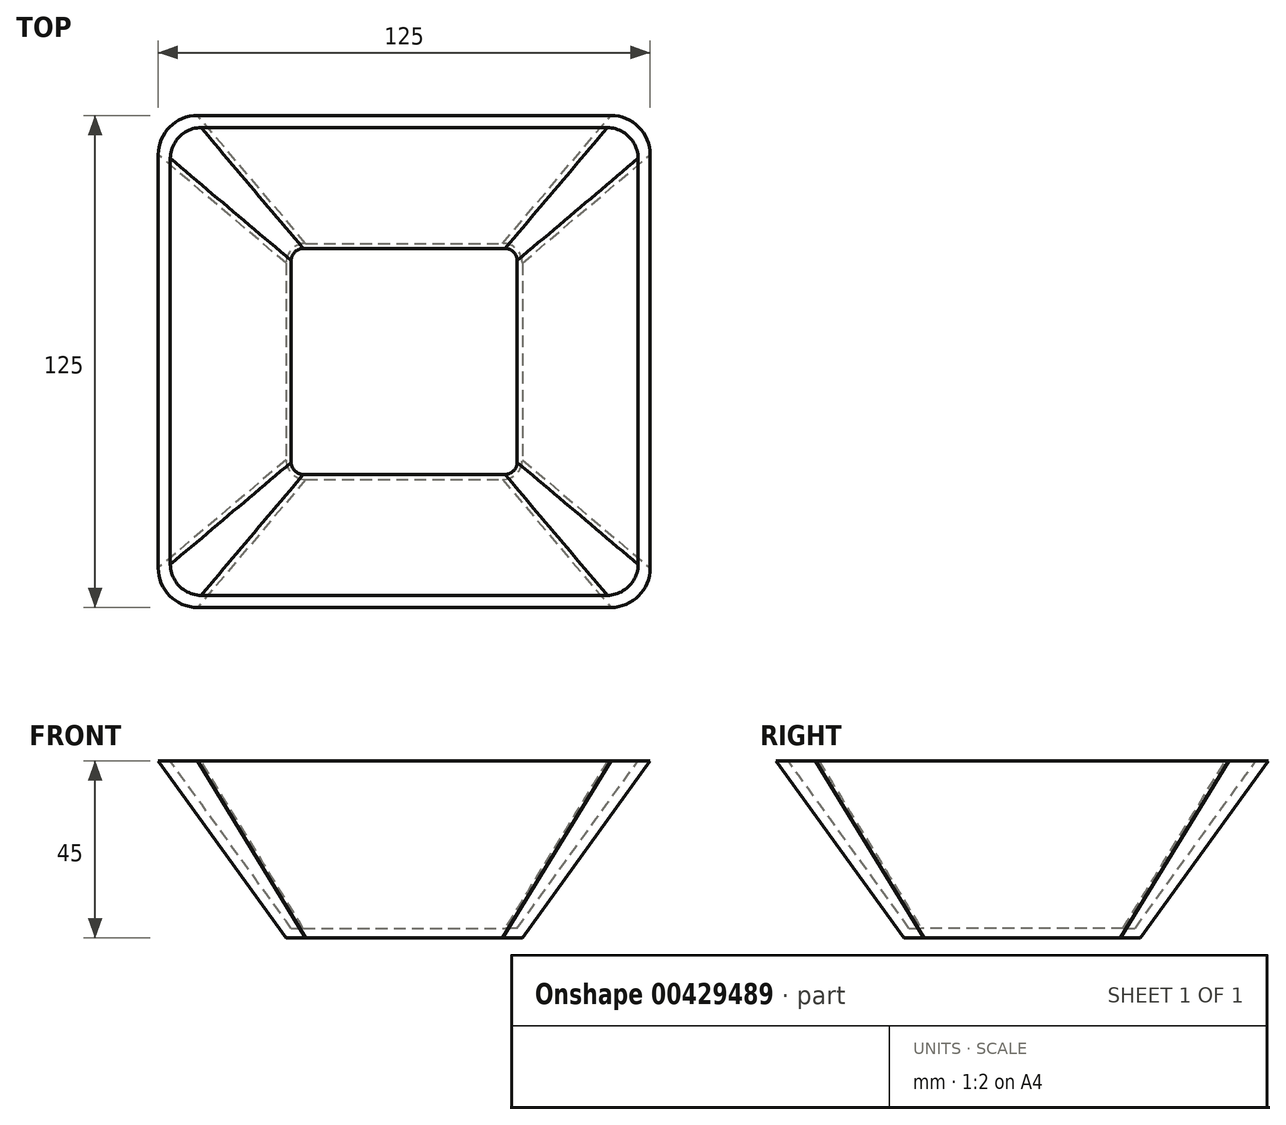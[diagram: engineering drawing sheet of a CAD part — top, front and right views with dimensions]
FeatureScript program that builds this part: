
annotation { "Feature Type Name" : "Feature", "Feature Type Description" : "" }
export const myFeature = defineFeature(function(context is Context, id is Id, definition is map)
    precondition{}
    {
        {
            var Q0;
            Q0=qCreatedBy(makeId("Top.planeOp"),FACE);
            var sketch = newSketch(context, id + "F0", { "sketchPlane" : qUnion([Q0])});
            skLineSegment(sketch, "E0.bottom", {"start": v(-25, 30) * mm, "end": v(25, 30) * mm});
            skLineSegment(sketch, "E0.top", {"start": v(-25, -30) * mm, "end": v(25, -30) * mm});
            skLineSegment(sketch, "E0.left", {"start": v(-30, 25) * mm, "end": v(-30, -25) * mm});
            skLineSegment(sketch, "E0.right", {"start": v(30, 25) * mm, "end": v(30, -25) * mm});
            skLineSegment(sketch, "E1", {"start": v(-30, -30) * mm, "end": v(30, 30) * mm, "construction": true});
            skPoint(sketch, "E2.visualSharp", {"position": v(30, 30) * mm});
            skArc(sketch, "E2.filletArc", {"start": v(30, 25) * mm, "mid": v(28.54, 28.54) * mm, "end": v(25, 30) * mm});
            skPoint(sketch, "E3.visualSharp", {"position": v(-30, 30) * mm});
            skArc(sketch, "E3.filletArc", {"start": v(-25, 30) * mm, "mid": v(-28.54, 28.54) * mm, "end": v(-30, 25) * mm});
            skPoint(sketch, "E4.visualSharp", {"position": v(30, -30) * mm});
            skArc(sketch, "E4.filletArc", {"start": v(25, -30) * mm, "mid": v(28.54, -28.54) * mm, "end": v(30, -25) * mm});
            skPoint(sketch, "E5.visualSharp", {"position": v(-30, -30) * mm});
            skArc(sketch, "E5.filletArc", {"start": v(-30, -25) * mm, "mid": v(-28.54, -28.54) * mm, "end": v(-25, -30) * mm});
            skSolve(sketch);
        }
        {
            var Q0;
            Q0=qCreatedBy(makeId("Top.planeOp"),FACE);
            cPlane(context, id + "F1", {"entities" : qUnion([Q0]), "cplaneType" : CPlaneType.OFFSET, "offset" : 45 * mm, "width" : 150 * mm, "height" : 150 * mm});
        }
        {
            var Q0;
            Q0=qCreatedBy(id+"F1.planeOp",FACE);
            var sketch = newSketch(context, id + "F2", { "sketchPlane" : qUnion([Q0])});
            skLineSegment(sketch, "E6.bottom", {"start": v(-52.5, 62.5) * mm, "end": v(52.5, 62.5) * mm});
            skLineSegment(sketch, "E6.top", {"start": v(-52.5, -62.5) * mm, "end": v(52.5, -62.5) * mm});
            skLineSegment(sketch, "E6.left", {"start": v(-62.5, 52.5) * mm, "end": v(-62.5, -52.5) * mm});
            skLineSegment(sketch, "E6.right", {"start": v(62.5, 52.5) * mm, "end": v(62.5, -52.5) * mm});
            skLineSegment(sketch, "E7", {"start": v(-62.5, 62.5) * mm, "end": v(62.5, -62.5) * mm, "construction": true});
            skPoint(sketch, "E8.visualSharp", {"position": v(62.5, 62.5) * mm});
            skArc(sketch, "E8.filletArc", {"start": v(62.5, 52.5) * mm, "mid": v(59.57, 59.57) * mm, "end": v(52.5, 62.5) * mm});
            skPoint(sketch, "E9.visualSharp", {"position": v(-62.5, 62.5) * mm});
            skArc(sketch, "E9.filletArc", {"start": v(-52.5, 62.5) * mm, "mid": v(-59.57, 59.57) * mm, "end": v(-62.5, 52.5) * mm});
            skPoint(sketch, "E10.visualSharp", {"position": v(-62.5, -62.5) * mm});
            skArc(sketch, "E10.filletArc", {"start": v(-62.5, -52.5) * mm, "mid": v(-59.57, -59.57) * mm, "end": v(-52.5, -62.5) * mm});
            skPoint(sketch, "E11.visualSharp", {"position": v(62.5, -62.5) * mm});
            skArc(sketch, "E11.filletArc", {"start": v(52.5, -62.5) * mm, "mid": v(59.57, -59.57) * mm, "end": v(62.5, -52.5) * mm});
            skSolve(sketch);
        }
        {
            var Q0;
            Q0=makeQuery(id+"F0.imprint","IMPRINT",FACE,{"disambiguationData":[TD([[makeQuery(id+"F0.imprint","IMPRINT",EDGE,{"derivedFrom":sQuery(id+"F0.wireOp",EDGE,"E0.bottom")}),-1.0]])]});
            var Q1;
            Q1=makeQuery(id+"F2.imprint","IMPRINT",FACE,{"disambiguationData":[TD([[makeQuery(id+"F2.imprint","IMPRINT",EDGE,{"derivedFrom":sQuery(id+"F2.wireOp",EDGE,"E6.bottom")}),-1.0]])]});
            loft(context, id + "F3", {"sheetProfilesArray" : [{ "sheetProfileEntities" : qUnion([Q0]) }, { "sheetProfileEntities" : qUnion([Q1]) }]});
        }
        {
            var Q0;
            Q0=makeQuery(id+"F3.opLoft","CAP_FACE",FACE,{"disambiguationData":[OSD([makeQuery(id+"F2.imprint","IMPRINT",FACE,{"disambiguationData":[TD([[makeQuery(id+"F2.imprint","IMPRINT",EDGE,{"derivedFrom":sQuery(id+"F2.wireOp",EDGE,"E6.bottom")}),-1.0]])]})])],"isStart":true});
            shell(context, id + "F4", {"entities" : qUnion([Q0]), "thickness" : 2.5 * mm});
        }
    });
